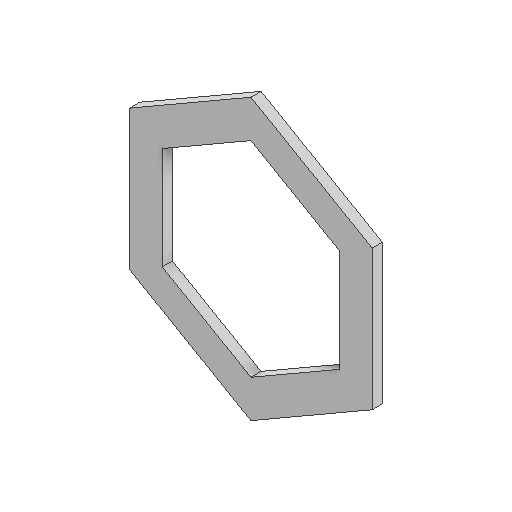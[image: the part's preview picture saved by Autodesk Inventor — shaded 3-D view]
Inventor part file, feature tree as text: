
AUTODESK INVENTOR PART (.ipt)
format: ipt  version: 2024.1 (Build 281209000, 209)  size: 94,720 bytes
history: native  units: in
note: dims shown in document units (in); Inventor stores cm internally (conversion verified against a paired STEP export)
features: other x3, sketch x1
ambient origin geometry x8: Origin, YZ Plane, XZ Plane, XY Plane, X Axis, Y Axis, Z Axis, Center Point
bodies: Solid1 (feature_tree)
feature tree (4):
  other  "Shaft Spacers V2.ipt"
  other  "Solid1::Shaft Spacers V2.ipt"
  other  "TaggingFeature1"
  sketch  "Sketch1"  dims[d0=0.3937in]
